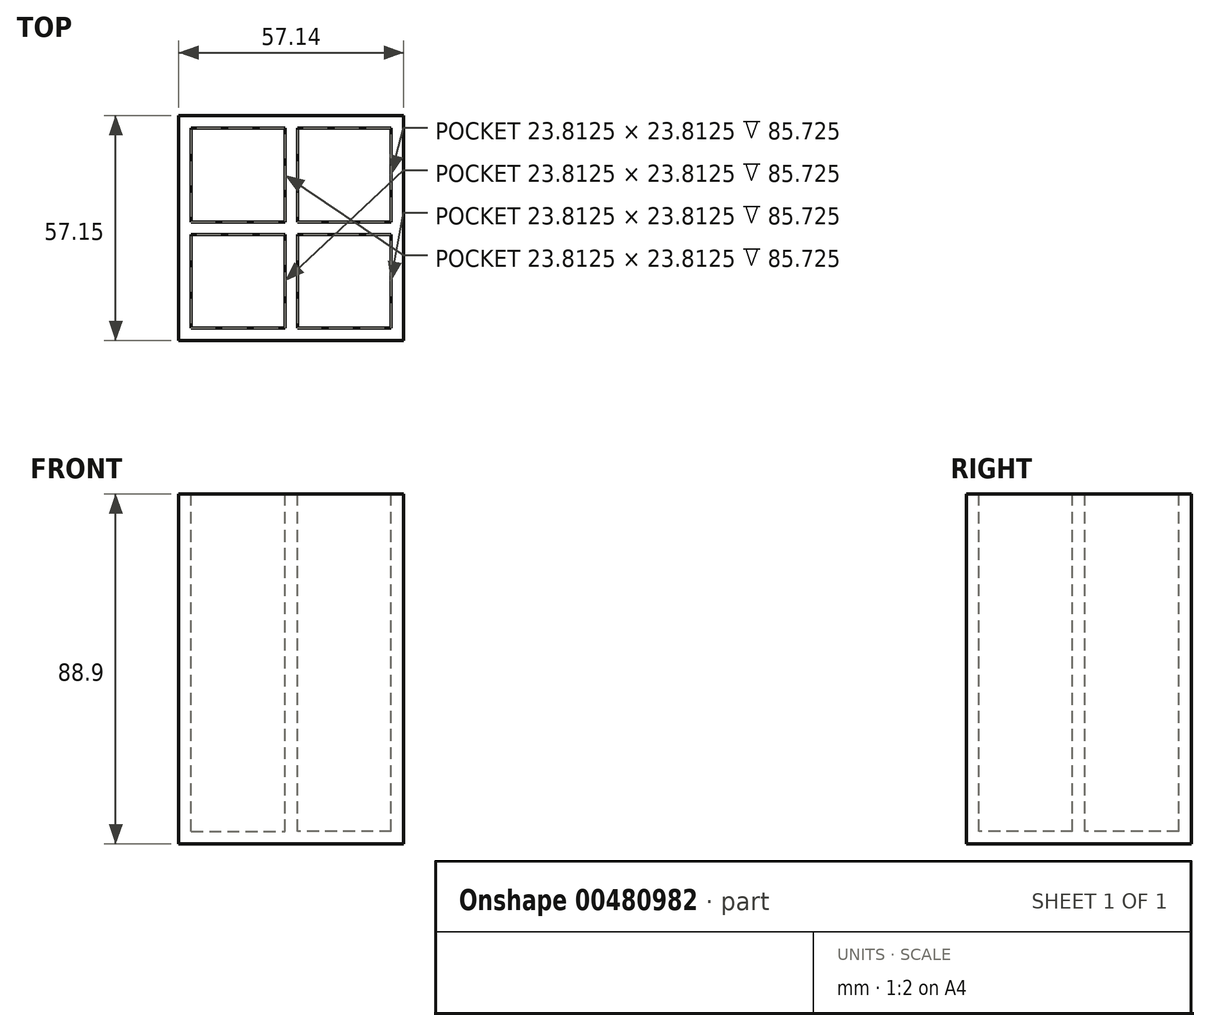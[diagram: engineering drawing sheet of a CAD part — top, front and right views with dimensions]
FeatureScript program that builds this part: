
annotation { "Feature Type Name" : "Feature", "Feature Type Description" : "" }
export const myFeature = defineFeature(function(context is Context, id is Id, definition is map)
    precondition{}
    {
        {
            var Q0;
            Q0=qCreatedBy(makeId("Front.planeOp"),FACE);
            var sketch = newSketch(context, id + "F0", { "sketchPlane" : qUnion([Q0])});
            skLineSegment(sketch, "E0.bottom", {"start": v(28.57, 44.45) * mm, "end": v(-28.58, 44.45) * mm});
            skLineSegment(sketch, "E0.top", {"start": v(28.58, -44.45) * mm, "end": v(-28.57, -44.45) * mm});
            skLineSegment(sketch, "E0.left", {"start": v(28.57, 44.45) * mm, "end": v(28.58, -44.45) * mm});
            skLineSegment(sketch, "E0.right", {"start": v(-28.58, 44.45) * mm, "end": v(-28.57, -44.45) * mm});
            skPoint(sketch, "E0.middle", {"position": v(0, 0) * mm});
            skSolve(sketch);
        }
        {
            var Q0;
            Q0=qSketchRegion(id+"F0",true);
            extrude(context, id + "F1", {"entities" : qUnion([Q0]), "depth" : 57.15 * mm});
        }
        {
            var Q0;
            Q0=makeQuery(id+"F1.opExtrude","SWEPT_FACE",FACE,{"disambiguationData":[OSD([sQuery(id+"F0.wireOp",EDGE,"E0.bottom")])]});
            var sketch = newSketch(context, id + "F2", { "sketchPlane" : qUnion([Q0])});
            skPoint(sketch, "E1.middle", {"position": v(0, 0) * mm});
            skLineSegment(sketch, "E2", {"start": v(25.4, -3.18) * mm, "end": v(1.59, -3.18) * mm});
            skLineSegment(sketch, "E3", {"start": v(-1.59, -3.18) * mm, "end": v(-25.4, -3.18) * mm});
            skLineSegment(sketch, "E4", {"start": v(1.59, -3.18) * mm, "end": v(1.59, -26.99) * mm});
            skLineSegment(sketch, "E5", {"start": v(-1.59, -3.18) * mm, "end": v(-1.59, -26.99) * mm});
            skLineSegment(sketch, "E6", {"start": v(25.4, -30.16) * mm, "end": v(25.4, -53.98) * mm});
            skLineSegment(sketch, "E7", {"start": v(1.59, -53.98) * mm, "end": v(25.4, -53.98) * mm});
            skLineSegment(sketch, "E8", {"start": v(-25.4, -3.17) * mm, "end": v(-25.4, -26.99) * mm});
            skLineSegment(sketch, "E9", {"start": v(-1.59, -53.98) * mm, "end": v(-25.4, -53.98) * mm});
            skLineSegment(sketch, "E10", {"start": v(25.4, -3.18) * mm, "end": v(25.4, -26.99) * mm});
            skLineSegment(sketch, "E11", {"start": v(25.4, -26.99) * mm, "end": v(1.59, -26.99) * mm});
            skLineSegment(sketch, "E12", {"start": v(25.4, -30.16) * mm, "end": v(1.59, -30.16) * mm});
            skLineSegment(sketch, "E13.bottom", {"start": v(-25.4, -30.16) * mm, "end": v(-1.59, -30.16) * mm});
            skLineSegment(sketch, "E13.top", {"start": v(-25.4, -53.98) * mm, "end": v(-1.59, -53.98) * mm});
            skLineSegment(sketch, "E13.left", {"start": v(-25.4, -30.16) * mm, "end": v(-25.4, -53.98) * mm});
            skLineSegment(sketch, "E13.right", {"start": v(-1.59, -30.16) * mm, "end": v(-1.59, -53.98) * mm});
            skLineSegment(sketch, "E14.top", {"start": v(25.4, -53.98) * mm, "end": v(1.59, -53.98) * mm});
            skLineSegment(sketch, "E14.right", {"start": v(1.59, -30.16) * mm, "end": v(1.59, -53.98) * mm});
            skLineSegment(sketch, "E15.left", {"start": v(25.4, -26.99) * mm, "end": v(25.4, -3.18) * mm});
            skLineSegment(sketch, "E15.right", {"start": v(1.59, -26.99) * mm, "end": v(1.59, -3.18) * mm});
            skLineSegment(sketch, "E16.bottom", {"start": v(-25.4, -3.18) * mm, "end": v(-1.59, -3.18) * mm});
            skLineSegment(sketch, "E16.top", {"start": v(-25.4, -26.99) * mm, "end": v(-1.59, -26.99) * mm});
            skLineSegment(sketch, "E16.left", {"start": v(-25.4, -3.18) * mm, "end": v(-25.4, -26.99) * mm});
            skLineSegment(sketch, "E17.trimOffspring", {"start": v(-1.59, -26.99) * mm, "end": v(-25.4, -26.99) * mm});
            skLineSegment(sketch, "E18.trimOffspring", {"start": v(-1.59, -30.16) * mm, "end": v(-25.4, -30.16) * mm});
            skSolve(sketch);
        }
        {
            var Q0;
            Q0=qSketchRegion(id+"F2",true);
            extrude(context, id + "F3", {"entities" : qUnion([Q0]), "operationType" : NewBodyOperationType.REMOVE, "oppositeDirection" : true, "depth" : 85.72 * mm});
        }
    });
